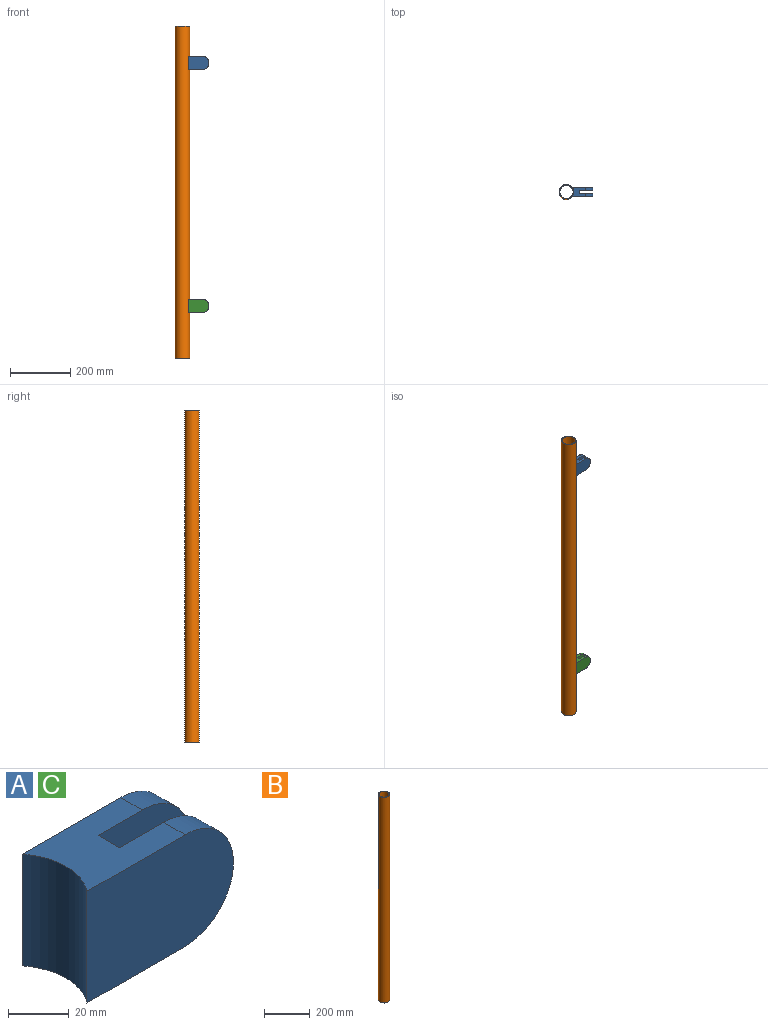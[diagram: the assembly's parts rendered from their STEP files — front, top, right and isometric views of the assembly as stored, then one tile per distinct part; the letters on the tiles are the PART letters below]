
ASSEMBLY  parts=3 mates=2
PART A: 10 faces, bbox 68.2x30x45 mm
  f0: plane 45x43mm, normal (0,-1,0), area 1717.7mm2, adj f5,f6,f7,f9
  f1: plane 68.22x45mm, normal (0,1,0), area 2852.8mm2, adj f4,f6,f7,f9
  f2: plane 68.22x45mm, normal (0,-1,0), area 2852.8mm2, adj f4,f6,f7,f8
  f3: plane 45x43mm, normal (0,1,0), area 1717.7mm2, adj f5,f6,f7,f8
  f4: cylinder r=24.15mm len=45mm, axis (0,0,-1), area 1456.6mm2, adj f1,f2,f6,f7
  f5: plane 45x10mm, normal (1,0,0), area 450mm2, adj f0,f3,f6,f7
  f6: plane 45.72x30mm, normal (0,0,1), area 1059.7mm2, adj f0,f1,f2,f3,f4,f5,f8,f9
  f7: plane 45.72x30mm, normal (0,0,-1), area 1059.7mm2, adj f0,f1,f2,f3,f4,f5,f8,f9
  f8: cylinder r=22.5mm len=45mm, axis (0,-1,0), area 706.9mm2, adj f2,f3,f6,f7
  f9: cylinder r=22.5mm len=45mm, axis (0,-1,0), area 706.9mm2, adj f0,f1,f6,f7
PART B: 4 faces, bbox 48.3x48.3x1100 mm
  f0: cylinder r=22.15mm len=1100mm, axis (0,0,-1), area 153089.8mm2, adj f2,f3
  f1: cylinder r=24.15mm len=1100mm, axis (0,0,-1), area 166912.8mm2, adj f2,f3
  f2: plane 48.3x48.3mm, normal (0,0,1), area 290.9mm2, adj f0,f1
  f3: plane 48.3x48.3mm, normal (0,0,-1), area 290.9mm2, adj f0,f1
PART C: same geometry as A
PLACE A rot(axis=(1,0,0),180deg) t=(0,0,1000)mm
PLACE B at identity fixed
PLACE C t=(0,0,150)mm
MATE fastened B.f1 <-> C.f4  axis (0,0,-1) through (0,0,550)mm
MATE fastened A.f4 <-> B.f1  axis (0,0,1) through (0,0,977.5)mm
